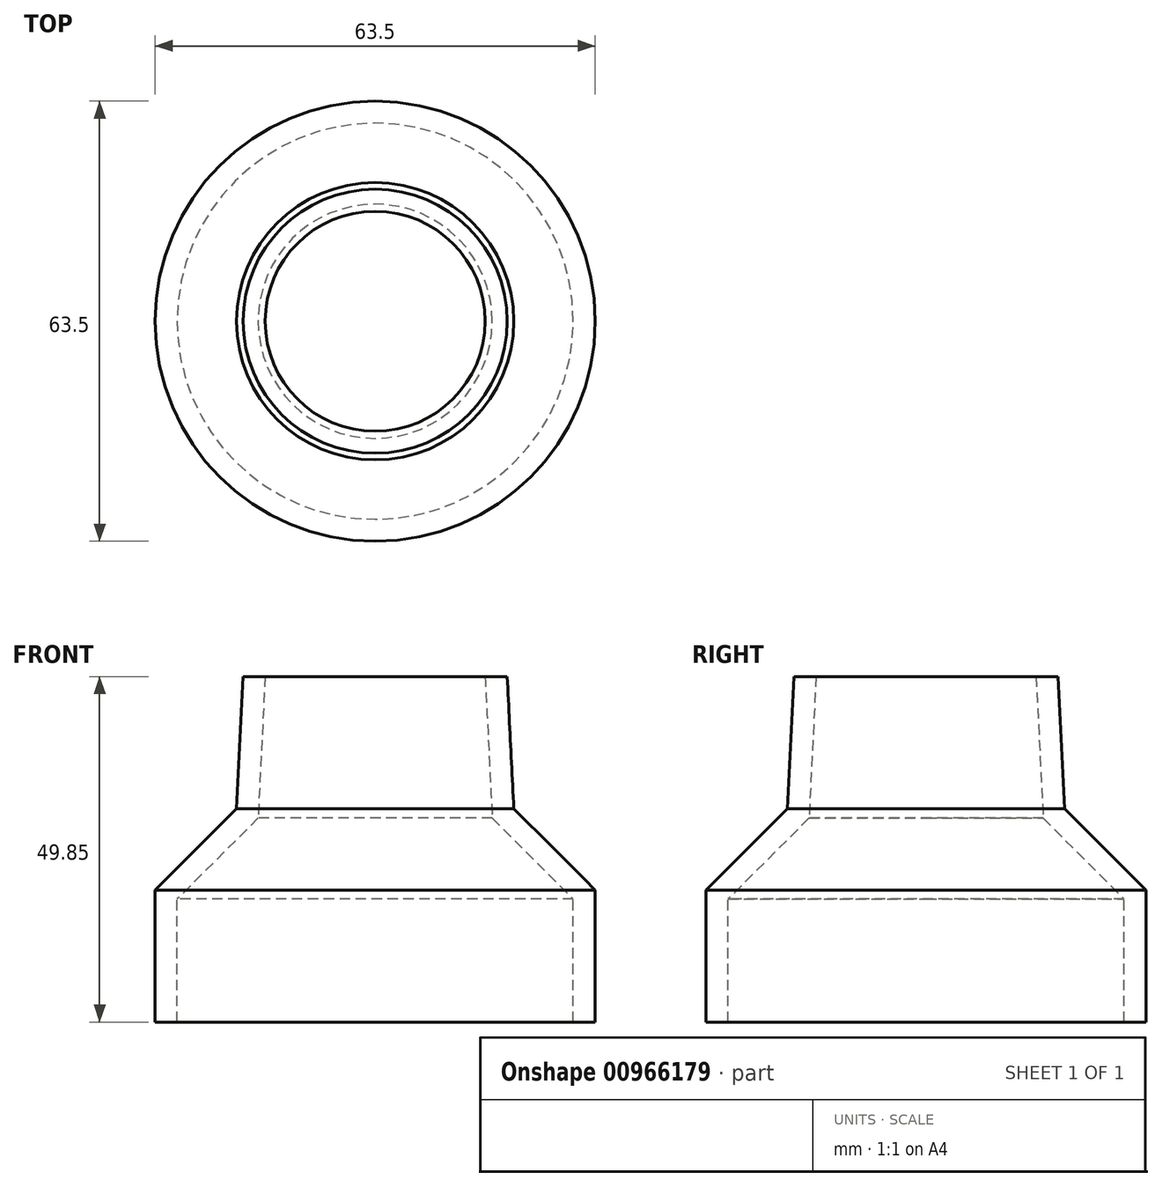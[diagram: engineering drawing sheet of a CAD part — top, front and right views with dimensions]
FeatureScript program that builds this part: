
annotation { "Feature Type Name" : "Feature", "Feature Type Description" : "" }
export const myFeature = defineFeature(function(context is Context, id is Id, definition is map)
    precondition{}
    {
        {
            var Q0;
            Q0=qCreatedBy(makeId("Front.planeOp"),FACE);
            var sketch = newSketch(context, id + "F0", { "sketchPlane" : qUnion([Q0])});
            skLineSegment(sketch, "E0", {"start": v(-19.05, 0) * mm, "end": v(-20, -19.05) * mm});
            skLineSegment(sketch, "E1", {"start": v(-20, -19.05) * mm, "end": v(-31.75, -30.8) * mm});
            skLineSegment(sketch, "E2", {"start": v(-31.75, -30.8) * mm, "end": v(-31.75, -49.85) * mm});
            skLineSegment(sketch, "E3", {"start": v(0, 0) * mm, "end": v(0, -64.35) * mm, "construction": true});
            skLineSegment(sketch, "E4", {"start": v(-19.53, -9.53) * mm, "end": v(0, -9.52) * mm, "construction": true});
            skPoint(sketch, "E4.endSnap0", {"position": v(-19.53, -9.53) * mm});
            skLineSegment(sketch, "E5.0", {"start": v(-28.57, -32.11) * mm, "end": v(-28.57, -49.85) * mm});
            skLineSegment(sketch, "E5.1", {"start": v(-16.9, -20.43) * mm, "end": v(-28.58, -32.11) * mm});
            skLineSegment(sketch, "E5.2", {"start": v(-15.87, 0) * mm, "end": v(-16.9, -20.43) * mm});
            skLineSegment(sketch, "E6", {"start": v(-19.05, 0) * mm, "end": v(-15.87, 0) * mm});
            skLineSegment(sketch, "E7", {"start": v(-31.75, -49.85) * mm, "end": v(-28.57, -49.85) * mm});
            skSolve(sketch);
        }
        {
            var Q0;
            Q0=qSketchRegion(id+"F0",true);
            var Q1;
            Q1=sQuery(id+"F0.wireOp",EDGE,"E3");
            revolve(context, id + "F1", {"surfaceOperationType" : NewSurfaceOperationType.NEW, "entities" : qUnion([Q0]), "axis" : qUnion([Q1]), "revolveType" : RevolveType.FULL});
        }
    });
